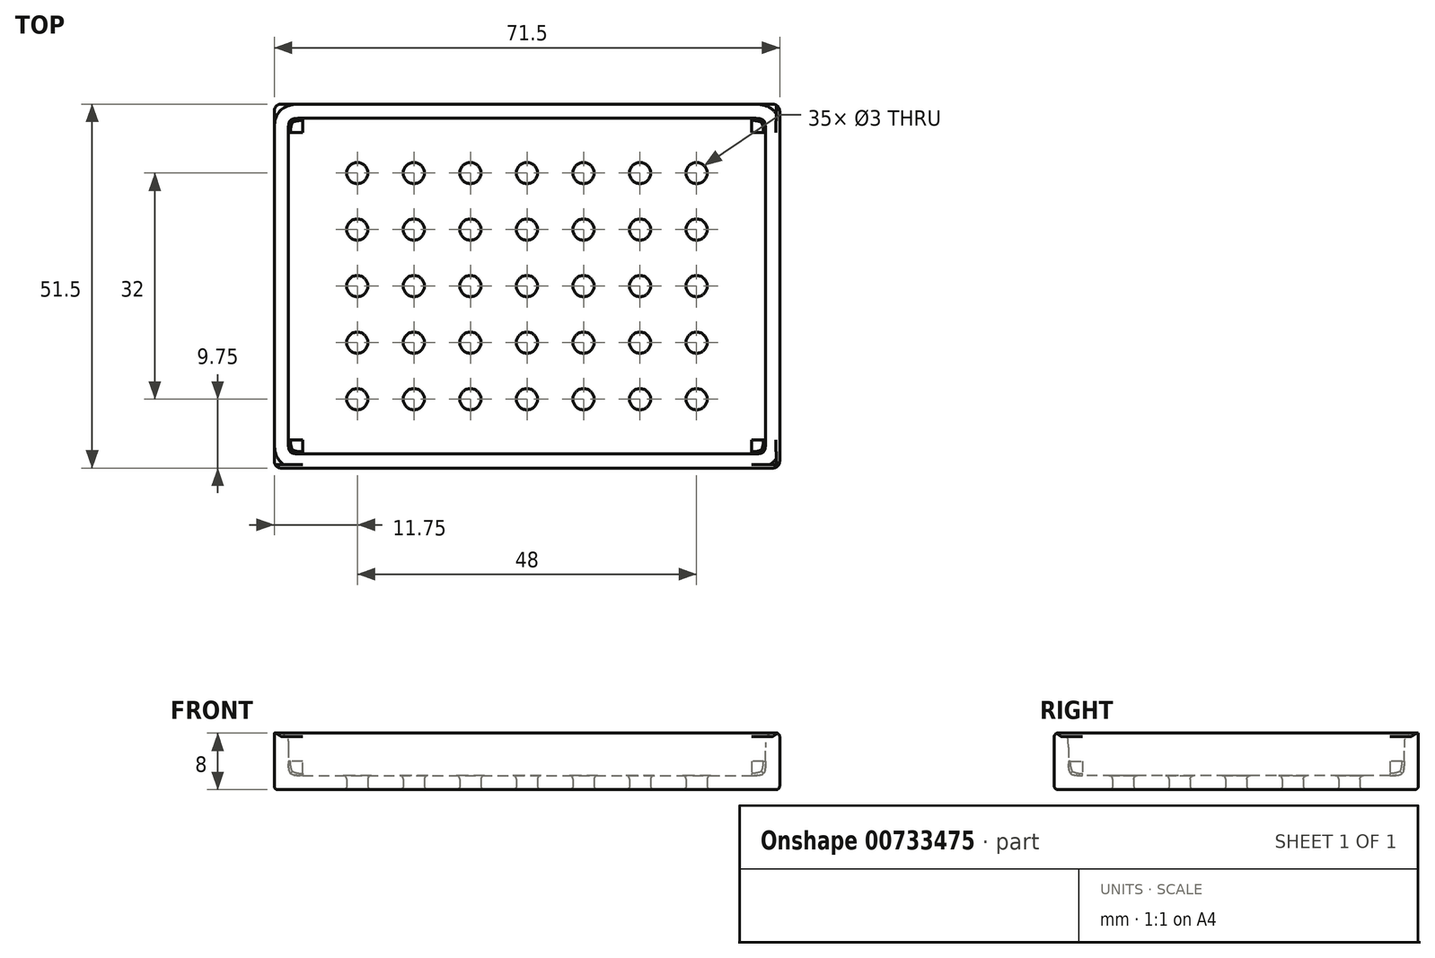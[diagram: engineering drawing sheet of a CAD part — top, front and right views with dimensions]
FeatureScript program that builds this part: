
annotation { "Feature Type Name" : "Feature", "Feature Type Description" : "" }
export const myFeature = defineFeature(function(context is Context, id is Id, definition is map)
    precondition{}
    {
        {
            var Q0;
            Q0=qCreatedBy(makeId("Top.planeOp"),FACE);
            var sketch = newSketch(context, id + "F0", { "sketchPlane" : qUnion([Q0])});
            skLineSegment(sketch, "E0.bottom", {"start": v(-35.75, 25.75) * mm, "end": v(35.75, 25.75) * mm});
            skLineSegment(sketch, "E0.top", {"start": v(-35.75, -25.75) * mm, "end": v(35.75, -25.75) * mm});
            skLineSegment(sketch, "E0.left", {"start": v(-35.75, 25.75) * mm, "end": v(-35.75, -25.75) * mm});
            skLineSegment(sketch, "E0.right", {"start": v(35.75, 25.75) * mm, "end": v(35.75, -25.75) * mm});
            skPoint(sketch, "E0.middle", {"position": v(0, 0) * mm});
            skSolve(sketch);
        }
        {
            var Q0;
            Q0 = qSketchRegion(id + "F0", true);
            extrude(context, id + "F1", {"entities" : qUnion([Q0]), "depth" : 8 * mm, "offsetDistance" : 25 * mm, "symmetric" : true});
        }
        {
            var Q0;
            Q0=makeQuery(id+"F1.opExtrude","CAP_FACE",FACE,{"disambiguationData":[OSD([sQuery(id+"F0.wireOp",EDGE,"E0.bottom"),sQuery(id+"F0.wireOp",EDGE,"E0.top"),sQuery(id+"F0.wireOp",EDGE,"E0.left"),sQuery(id+"F0.wireOp",EDGE,"E0.right")])],"isStart":false});
            shell(context, id + "F2", {"entities" : qUnion([Q0]), "thickness" : 2 * mm});
        }
        {
            var Q0;
            {var subQ0=sQuery(id+"F0.wireOp",EDGE,"E0.top");Q0=makeQuery(id+"F2.opShell","OFFSET_EDGE",EDGE,{"disambiguationData":[OSD([subQ0]),TDD([makeQuery(id+"F1.opExtrude","CAP_EDGE",EDGE,{"disambiguationData":[OSD([subQ0])],"isStart":false})])]});}
            var Q1;
            Q1=makeQuery(id+"F2.opShell","OFFSET_FACE",FACE,{"disambiguationData":[OSD([sQuery(id+"F0.wireOp",EDGE,"E0.bottom"),sQuery(id+"F0.wireOp",EDGE,"E0.top"),sQuery(id+"F0.wireOp",EDGE,"E0.left"),sQuery(id+"F0.wireOp",EDGE,"E0.right")])]});
            var Q2;
            {var subQ0=sQuery(id+"F0.wireOp",EDGE,"E0.right");Q2=makeQuery(id+"F2.opShell","OFFSET_EDGE",EDGE,{"disambiguationData":[OSD([subQ0]),TDD([makeQuery(id+"F1.opExtrude","CAP_EDGE",EDGE,{"disambiguationData":[OSD([subQ0])],"isStart":false})])]});}
            var Q3;
            {var subQ0=sQuery(id+"F0.wireOp",EDGE,"E0.left");Q3=makeQuery(id+"F2.opShell","OFFSET_EDGE",EDGE,{"disambiguationData":[OSD([subQ0]),TDD([makeQuery(id+"F1.opExtrude","CAP_EDGE",EDGE,{"disambiguationData":[OSD([subQ0])],"isStart":false})])]});}
            var Q4;
            {var subQ0=sQuery(id+"F0.wireOp",EDGE,"E0.bottom");Q4=makeQuery(id+"F2.opShell","OFFSET_EDGE",EDGE,{"disambiguationData":[OSD([subQ0]),TDD([makeQuery(id+"F1.opExtrude","CAP_EDGE",EDGE,{"disambiguationData":[OSD([subQ0])],"isStart":false})])]});}
            var Q5;
            Q5=makeQuery(id+"F2.opShell","OFFSET_EDGE",EDGE,{"disambiguationData":[OSD([sQuery(id+"F0.wireOp",EDGE,"E0.top"),sQuery(id+"F0.wireOp",EDGE,"E0.right")])]});
            var Q6;
            Q6=makeQuery(id+"F2.opShell","OFFSET_EDGE",EDGE,{"disambiguationData":[OSD([sQuery(id+"F0.wireOp",EDGE,"E0.bottom"),sQuery(id+"F0.wireOp",EDGE,"E0.right")])]});
            var Q7;
            Q7=makeQuery(id+"F2.opShell","OFFSET_EDGE",EDGE,{"disambiguationData":[OSD([sQuery(id+"F0.wireOp",EDGE,"E0.top"),sQuery(id+"F0.wireOp",EDGE,"E0.left")])]});
            var Q8;
            Q8=makeQuery(id+"F2.opShell","OFFSET_EDGE",EDGE,{"disambiguationData":[OSD([sQuery(id+"F0.wireOp",EDGE,"E0.bottom"),sQuery(id+"F0.wireOp",EDGE,"E0.left")])]});
            fillet(context, id + "F3", {"entities" : qUnion([Q0, Q1, Q2, Q3, Q4, Q5, Q6, Q7, Q8]), "radius" : 2 * mm, "tangentPropagation" : true, "rho" : 0.7, "crossSection" : FilletCrossSection.CONIC, "allowEdgeOverflow" : false});
        }
        {
            var Q0;
            Q0=makeQuery(id+"F1.opExtrude","CAP_FACE",FACE,{"disambiguationData":[OSD([sQuery(id+"F0.wireOp",EDGE,"E0.bottom"),sQuery(id+"F0.wireOp",EDGE,"E0.top"),sQuery(id+"F0.wireOp",EDGE,"E0.left"),sQuery(id+"F0.wireOp",EDGE,"E0.right")])],"isStart":true});
            var sketch = newSketch(context, id + "F4", { "sketchPlane" : qUnion([Q0])});
            skCircle(sketch, "E1", {"center": v(0, 0) * mm, "radius": 1.5 * mm});
            skCircle(sketch, "E2.0.1.0", {"center": v(0, 8) * mm, "radius": 1.5 * mm});
            skCircle(sketch, "E2.0.2.0", {"center": v(0, 16) * mm, "radius": 1.5 * mm});
            skCircle(sketch, "E2.1.0.0", {"center": v(8, 0) * mm, "radius": 1.5 * mm});
            skCircle(sketch, "E2.1.1.0", {"center": v(8, 8) * mm, "radius": 1.5 * mm});
            skCircle(sketch, "E2.1.2.0", {"center": v(8, 16) * mm, "radius": 1.5 * mm});
            skCircle(sketch, "E2.2.0.0", {"center": v(16, 0) * mm, "radius": 1.5 * mm});
            skCircle(sketch, "E2.2.1.0", {"center": v(16, 8) * mm, "radius": 1.5 * mm});
            skCircle(sketch, "E2.2.2.0", {"center": v(16, 16) * mm, "radius": 1.5 * mm});
            skCircle(sketch, "E2.3.0.0", {"center": v(24, 0) * mm, "radius": 1.5 * mm});
            skCircle(sketch, "E2.3.1.0", {"center": v(24, 8) * mm, "radius": 1.5 * mm});
            skCircle(sketch, "E2.3.2.0", {"center": v(24, 16) * mm, "radius": 1.5 * mm});
            skLineSegment(sketch, "E2.direction1", {"start": v(0, 0) * mm, "end": v(8, 0) * mm, "construction": true});
            skLineSegment(sketch, "E2.direction2", {"start": v(0, 0) * mm, "end": v(0, 8) * mm, "construction": true});
            skCircle(sketch, "E3.MirrorC", {"center": v(-8, 16) * mm, "radius": 1.5 * mm});
            skCircle(sketch, "E4.MirrorC", {"center": v(-8, 8) * mm, "radius": 1.5 * mm});
            skCircle(sketch, "E5.MirrorC", {"center": v(-24, 0) * mm, "radius": 1.5 * mm});
            skLineSegment(sketch, "E6.MirrorCS", {"start": v(0, 0) * mm, "end": v(-8, 0) * mm, "construction": true});
            skCircle(sketch, "E7.MirrorC", {"center": v(-16, 0) * mm, "radius": 1.5 * mm});
            skCircle(sketch, "E8.MirrorC", {"center": v(-16, 8) * mm, "radius": 1.5 * mm});
            skCircle(sketch, "E9.MirrorC", {"center": v(-16, 16) * mm, "radius": 1.5 * mm});
            skCircle(sketch, "E10.MirrorC", {"center": v(-8, 0) * mm, "radius": 1.5 * mm});
            skCircle(sketch, "E11.MirrorC", {"center": v(-24, 8) * mm, "radius": 1.5 * mm});
            skCircle(sketch, "E12.MirrorC", {"center": v(-24, 16) * mm, "radius": 1.5 * mm});
            skCircle(sketch, "E13.MirrorC", {"center": v(0, -8) * mm, "radius": 1.5 * mm});
            skCircle(sketch, "E14.MirrorC", {"center": v(0, -16) * mm, "radius": 1.5 * mm});
            skCircle(sketch, "E15.MirrorC", {"center": v(-8, -8) * mm, "radius": 1.5 * mm});
            skCircle(sketch, "E16.MirrorC", {"center": v(-24, -16) * mm, "radius": 1.5 * mm});
            skCircle(sketch, "E17.MirrorC", {"center": v(24, -8) * mm, "radius": 1.5 * mm});
            skCircle(sketch, "E18.MirrorC", {"center": v(24, -16) * mm, "radius": 1.5 * mm});
            skCircle(sketch, "E19.MirrorC", {"center": v(-8, -16) * mm, "radius": 1.5 * mm});
            skCircle(sketch, "E20.MirrorC", {"center": v(16, -8) * mm, "radius": 1.5 * mm});
            skCircle(sketch, "E21.MirrorC", {"center": v(-16, -16) * mm, "radius": 1.5 * mm});
            skCircle(sketch, "E22.MirrorC", {"center": v(8, -16) * mm, "radius": 1.5 * mm});
            skCircle(sketch, "E23.MirrorC", {"center": v(8, -8) * mm, "radius": 1.5 * mm});
            skCircle(sketch, "E24.MirrorC", {"center": v(-16, -8) * mm, "radius": 1.5 * mm});
            skCircle(sketch, "E25.MirrorC", {"center": v(-24, -8) * mm, "radius": 1.5 * mm});
            skCircle(sketch, "E26.MirrorC", {"center": v(16, -16) * mm, "radius": 1.5 * mm});
            skSolve(sketch);
        }
        {
            var Q0;
            Q0 = qSketchRegion(id + "F4", true);
            extrude(context, id + "F5", {"entities" : qUnion([Q0]), "operationType" : NewBodyOperationType.REMOVE, "endBound" : BoundingType.THROUGH_ALL, "oppositeDirection" : true, "depth" : 25 * mm, "offsetDistance" : 25 * mm});
        }
        {
            var Q0;
            Q0=makeQuery(id+"F1.opExtrude","SWEPT_EDGE",EDGE,{"disambiguationData":[OSD([sQuery(id+"F0.wireOp",EDGE,"E0.top"),sQuery(id+"F0.wireOp",EDGE,"E0.left")])]});
            var Q1;
            Q1=makeQuery(id+"F1.opExtrude","SWEPT_EDGE",EDGE,{"disambiguationData":[OSD([sQuery(id+"F0.wireOp",EDGE,"E0.bottom"),sQuery(id+"F0.wireOp",EDGE,"E0.left")])]});
            var Q2;
            Q2=makeQuery(id+"F1.opExtrude","SWEPT_EDGE",EDGE,{"disambiguationData":[OSD([sQuery(id+"F0.wireOp",EDGE,"E0.bottom"),sQuery(id+"F0.wireOp",EDGE,"E0.right")])]});
            var Q3;
            Q3=makeQuery(id+"F1.opExtrude","SWEPT_EDGE",EDGE,{"disambiguationData":[OSD([sQuery(id+"F0.wireOp",EDGE,"E0.top"),sQuery(id+"F0.wireOp",EDGE,"E0.right")])]});
            fillet(context, id + "F6", {"entities" : qUnion([Q0, Q1, Q2, Q3]), "radius" : 1 * mm, "tangentPropagation" : true, "allowEdgeOverflow" : false});
        }
        {
            var Q0;
            Q0=makeQuery(id+"F1.opExtrude","CAP_EDGE",EDGE,{"disambiguationData":[OSD([sQuery(id+"F0.wireOp",EDGE,"E0.top")])],"isStart":true});
            var Q1;
            {var subQ0=sQuery(id+"F0.wireOp",EDGE,"E0.top");Q1=makeQuery(id+"F3.opFillet","BLEND_EDGE",EDGE,{"blendedFrom":[makeQuery(id+"F2.opShell","OFFSET_EDGE",EDGE,{"disambiguationData":[OSD([subQ0]),TDD([makeQuery(id+"F1.opExtrude","CAP_EDGE",EDGE,{"disambiguationData":[OSD([subQ0])],"isStart":false})])]}),makeQuery(id+"F1.opExtrude","SWEPT_FACE",FACE,{"disambiguationData":[OSD([subQ0])]})],"blendedInto":[makeQuery(id+"F1.opExtrude","SWEPT_FACE",FACE,{"disambiguationData":[OSD([subQ0])]})]});}
            var Q2;
            {var subQ0=sQuery(id+"F0.wireOp",EDGE,"E0.right");Q2=makeQuery(id+"F3.opFillet","BLEND_EDGE",EDGE,{"blendedFrom":[makeQuery(id+"F2.opShell","OFFSET_EDGE",EDGE,{"disambiguationData":[OSD([subQ0]),TDD([makeQuery(id+"F1.opExtrude","CAP_EDGE",EDGE,{"disambiguationData":[OSD([subQ0])],"isStart":false})])]}),makeQuery(id+"F1.opExtrude","SWEPT_FACE",FACE,{"disambiguationData":[OSD([subQ0])]})],"blendedInto":[makeQuery(id+"F1.opExtrude","SWEPT_FACE",FACE,{"disambiguationData":[OSD([subQ0])]})]});}
            var Q3;
            Q3=makeQuery(id+"F2.opShell","OFFSET_FACE",FACE,{"disambiguationData":[OSD([sQuery(id+"F0.wireOp",EDGE,"E0.bottom"),sQuery(id+"F0.wireOp",EDGE,"E0.top"),sQuery(id+"F0.wireOp",EDGE,"E0.left"),sQuery(id+"F0.wireOp",EDGE,"E0.right")])]});
            var Q4;
            Q4=makeQuery(id+"F1.opExtrude","CAP_FACE",FACE,{"disambiguationData":[OSD([sQuery(id+"F0.wireOp",EDGE,"E0.bottom"),sQuery(id+"F0.wireOp",EDGE,"E0.top"),sQuery(id+"F0.wireOp",EDGE,"E0.left"),sQuery(id+"F0.wireOp",EDGE,"E0.right")])],"isStart":true});
            fillet(context, id + "F7", {"entities" : qUnion([Q0, Q1, Q2, Q3, Q4]), "radius" : 0.5 * mm, "tangentPropagation" : true, "allowEdgeOverflow" : false});
        }
    });
